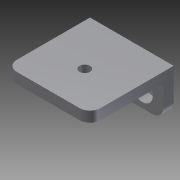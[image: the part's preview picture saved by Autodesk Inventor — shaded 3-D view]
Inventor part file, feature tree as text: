
AUTODESK INVENTOR PART (.ipt)
format: ipt  version: 2012 (Build 160160000, 160)  size: 112,128 bytes
history: native  units: in
note: dims shown in document units (in); Inventor stores cm internally (conversion verified against a paired STEP export)
features: extrude x3, sketch x3, fillet x1
ambient origin geometry x8: Origin, YZ Plane, XZ Plane, XY Plane, X Axis, Y Axis, Z Axis, Center Point
bodies: Solid1 (feature_tree)
feature tree (7):
  extrude  "Extrusion1"  Depth=0.5in
  extrude  "Extrusion2"  Depth=0.25in
  extrude  "Extrusion3"  Depth=0.25in
  fillet  "Fillet1"  Radius=0.125in
  sketch  "Sketch1"  dims[d0=1.0in d1=0.5in]
  sketch  "Sketch2"  dims[d2=0.25in d3=0.25in]
  sketch  "Sketch3"  dims[d5=0.25in d6=0.25in d8=0.125in d9=0.0in d10=0.125in d11=0.875in d12=0.0in d13=0.1875in d14=0.1875in d15=0.125in d16=0.875in d17=0.0in d18=0.125in]
